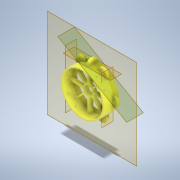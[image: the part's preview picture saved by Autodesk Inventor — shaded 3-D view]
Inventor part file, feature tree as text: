
AUTODESK INVENTOR PART (.ipt)
format: ipt  version: 2021.3 (Build 253353010, 353A)  size: 408,064 bytes
history: native  units: in
note: dims shown in document units (in); Inventor stores cm internally (conversion verified against a paired STEP export)
features: extrude x12, sketch x12, plane x5, pattern_circular x4, fillet x2, mirror x2
ambient origin geometry x8: Origin, YZ Plane, XZ Plane, XY Plane, X Axis, Y Axis, Z Axis, Center Point
bodies: Solid1 (feature_tree)
feature tree (37):
  extrude  "Extrusion1"  Depth=4.25in
  plane  "Work Plane1"
  plane  "Work Plane2"
  extrude  "Extrusion3"  Depth=2.125in
  fillet  "Fillet1"  Radius=2.125in
  extrude  "Extrusion4"  TaperAngle=0.0deg  [1 undecoded]
  pattern_circular  "Circular Pattern2"  Count=2 Angle=360.0deg
  plane  "Work Plane3"
  extrude  "Extrusion5"  Depth=1.0in
  extrude  "Extrusion6"  Depth=0.5in
  fillet  "Fillet2"  [1 undecoded]
  extrude  "Extrusion7"  Depth=0.5in TaperAngle=0.0deg
  pattern_circular  "Circular Pattern3"  [2 undecoded]
  plane  "Work Plane4"
  extrude  "Extrusion8"  Depth=0.2in
  extrude  "Extrusion9"  Depth=0.5in TaperAngle=0.0deg
  extrude  "Extrusion10"  Depth=0.5in TaperAngle=360.0deg
  extrude  "Extrusion11"  Depth=0.25in
  mirror  "Mirror1"
  extrude  "Extrusion12"  Depth=0.125in
  plane  "Work Plane5"
  extrude  "Extrusion13"  Depth=0.25in
  pattern_circular  "Circular Pattern5"  [2 undecoded]
  mirror  "Mirror2"
  pattern_circular  "Circular Pattern6"  [2 undecoded]
  sketch  "Sketch1"  dims[d0=4.0in d1=4.25in]
  sketch  "Sketch3"  dims[d2=1.0in d3=0.0in d4=1.5in d10=2.125in]
  sketch  "Sketch4"  dims[d11=0.25in d12=0.0in]
  sketch  "Sketch5"  dims[d13=0.5in d14=0.0in]
  sketch  "Sketch6"  dims[d15=0.5in]
  sketch  "Sketch7"  dims[d16=0.125in]
  sketch  "Sketch10"  dims[d17=0.2in]
  sketch  "Sketch11"  dims[d18=0.5in d19=0.0in d20=0.7874in d21=360.0deg]
  sketch  "Sketch12"  dims[d23=-2.125in d24=1.0in]
  sketch  "Sketch13"  dims[d25=0.25in d26=0.5in d27=0.0in]
  sketch  "Sketch14"  dims[d28=0.1in d29=0.0in d30=0.5in d31=0.0in]
  sketch  "Sketch15"  dims[d32=0.5in d33=0.25in d34=0.2in d35=0.5in d36=0.0in d37=2.3622in d38=360.0deg d40=0.25in d41=0.125in d42=0.25in d43=0.2in d54=0.5312in d55=0.25in d56=4.0in d57=4.0in d58=45.0deg d59=0.125in d60=4.0in d61=135.0deg d62=0.125in d63=4.0in d64=0.0in d65=0.125in d66=0.8661in d67=1.0236in d68=0.3543in d69=0.0in d70=0.5512in d71=0.0787in d72=0.0in d75=0.45in d76=0.2in d77=0.0in d81=0.1in d82=0.0in d83=0.5in d84=0.0in d85=90.0deg d86=0.125in d87=0.675in d88=0.3375in d91=0.1416in d92=0.1416in d93=0.5in d94=0.0in d95=1.9685in d96=120.0deg d98=2.3622in d99=360.0deg d53=0.0344in]
note: 8 required parameter values undecoded (feature->parameter linkage not recoverable at this tier; creation-order binding heuristic only, values carry confidence <= 0.55)
